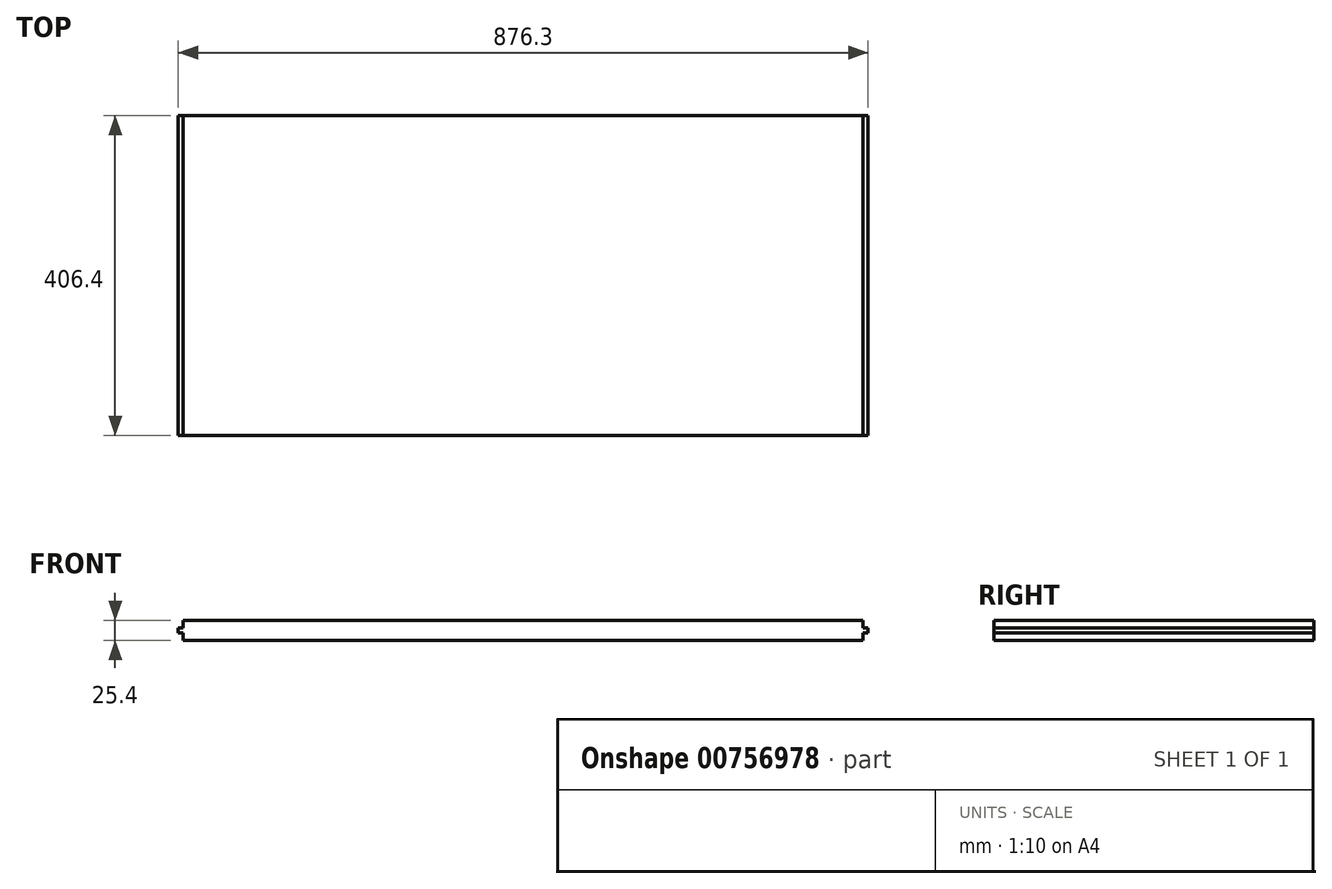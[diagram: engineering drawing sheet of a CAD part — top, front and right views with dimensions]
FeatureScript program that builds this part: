
annotation { "Feature Type Name" : "Feature", "Feature Type Description" : "" }
export const myFeature = defineFeature(function(context is Context, id is Id, definition is map)
    precondition{}
    {
        {
            var Q0;
            Q0=qCreatedBy(makeId("Front.planeOp"),FACE);
            var sketch = newSketch(context, id + "F0", { "sketchPlane" : qUnion([Q0])});
            skLineSegment(sketch, "E0.bottom", {"start": v(431.8, 12.7) * mm, "end": v(-431.8, 12.7) * mm});
            skLineSegment(sketch, "E0.top", {"start": v(431.8, -12.7) * mm, "end": v(-431.8, -12.7) * mm});
            skLineSegment(sketch, "E0.left", {"start": v(431.8, 12.7) * mm, "end": v(431.8, -12.7) * mm});
            skLineSegment(sketch, "E0.right", {"start": v(-431.8, 12.7) * mm, "end": v(-431.8, -12.7) * mm});
            skPoint(sketch, "E0.middle", {"position": v(0, 0) * mm});
            skLineSegment(sketch, "E1.bottom", {"start": v(-425.45, 3.18) * mm, "end": v(-438.15, 3.18) * mm});
            skLineSegment(sketch, "E1.top", {"start": v(-425.45, -3.17) * mm, "end": v(-438.15, -3.17) * mm});
            skLineSegment(sketch, "E1.left", {"start": v(-425.45, 3.18) * mm, "end": v(-425.45, -3.17) * mm});
            skLineSegment(sketch, "E1.right", {"start": v(-438.15, 3.18) * mm, "end": v(-438.15, -3.17) * mm});
            skPoint(sketch, "E1.middle", {"position": v(-431.8, 0) * mm});
            skLineSegment(sketch, "E2.bottom", {"start": v(438.15, 3.17) * mm, "end": v(425.45, 3.17) * mm});
            skLineSegment(sketch, "E2.top", {"start": v(438.15, -3.18) * mm, "end": v(425.45, -3.18) * mm});
            skLineSegment(sketch, "E2.left", {"start": v(438.15, 3.17) * mm, "end": v(438.15, -3.18) * mm});
            skLineSegment(sketch, "E2.right", {"start": v(425.45, 3.17) * mm, "end": v(425.45, -3.18) * mm});
            skPoint(sketch, "E2.middle", {"position": v(431.8, 0) * mm});
            skSolve(sketch);
        }
        {
            var Q0;
            Q0=qSketchRegion(id+"F0",true);
            extrude(context, id + "F1", {"entities" : qUnion([Q0]), "endBound" : BoundingType.SYMMETRIC, "depth" : 406.4 * mm});
        }
    });
